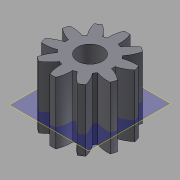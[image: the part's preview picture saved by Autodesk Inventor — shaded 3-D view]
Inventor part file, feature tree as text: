
AUTODESK INVENTOR PART (.ipt)
format: ipt  version: 2015 (Build 190159000, 159)  size: 167,424 bytes
history: native  units: in
note: dims shown in document units (in); Inventor stores cm internally (conversion verified against a paired STEP export)
features: other x13, sketch x3, plane x2
ambient origin geometry x8: Origin, YZ Plane, XZ Plane, XY Plane, X Axis, Y Axis, Z Axis, Center Point
bodies: Solid1 (feature_tree)
feature tree (18):
  other  "Spur Gear1"
  other  "Solid1::Spur Gear1"
  other  "TaggingFeature1"
  sketch  "Sketch1"  dims[d0=0.3937in]
  sketch  "Sketch2"  dims[d16=0.4724in d17=0.0in d41=0.0in d43=0.4724in d46=0.4724in d47=0.0in d48=0.0in]
  sketch  "Sketch3"
  plane  "XZ Plane_1"
  plane  "Work Plane2"
  other  "Z Axis_1"
  other  "Srf1"
  other  "Srf1::Derived"
  other  "Distance iMate"
  other  "Align iMate"
  other  "Mesh iMate"
  other  "Axis iMate"
  other  "Position iMate"
  other  "Mesh iMate2"
  other  "Start plane iMate"
